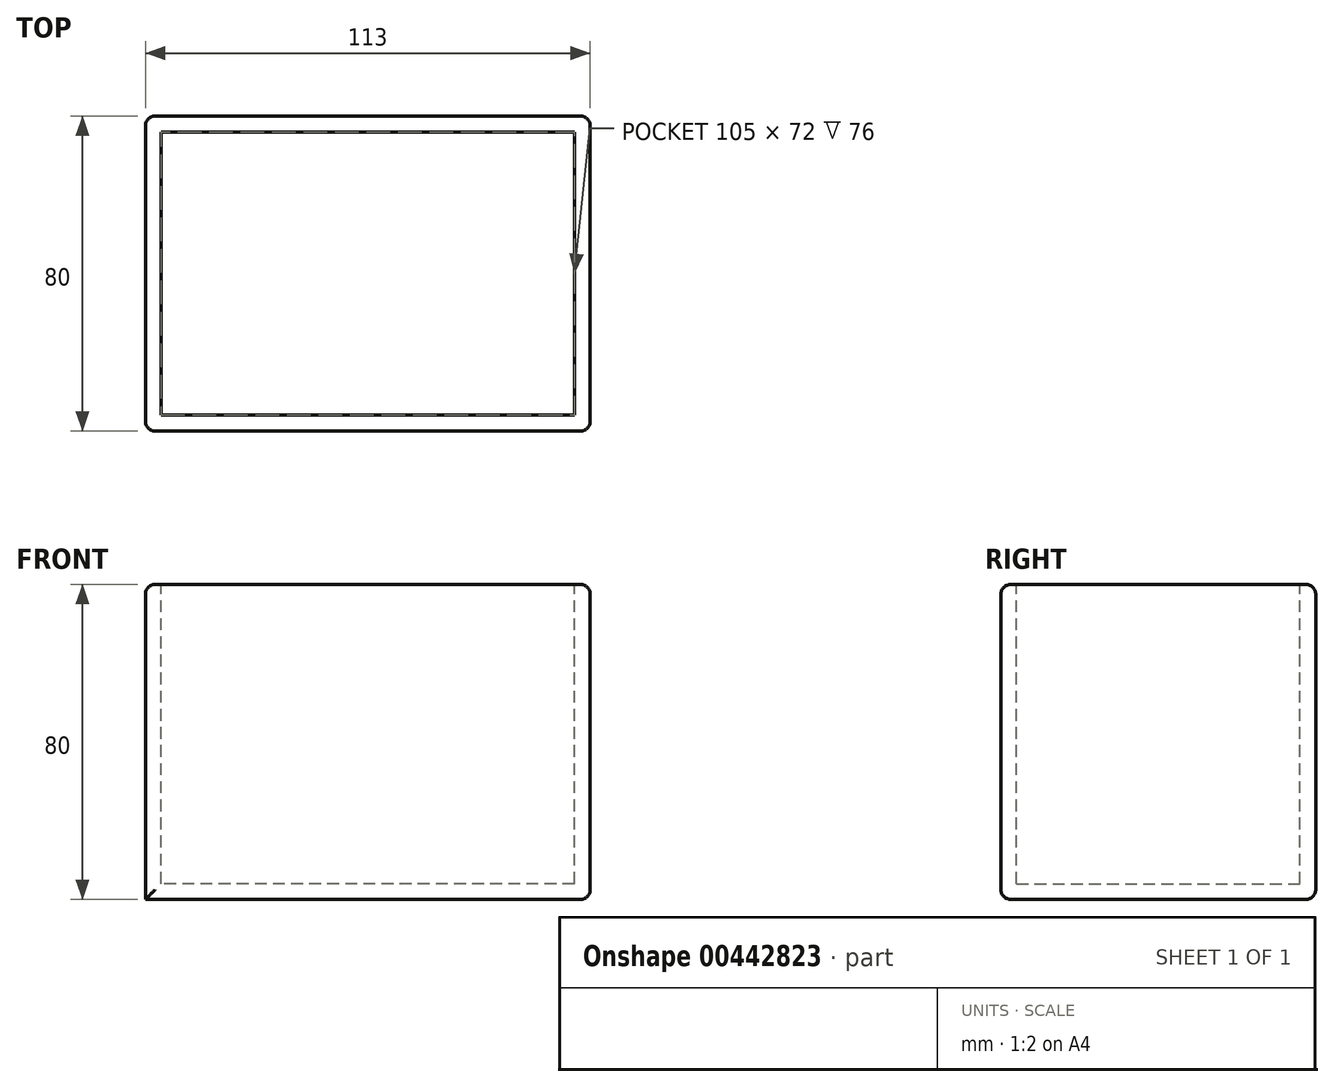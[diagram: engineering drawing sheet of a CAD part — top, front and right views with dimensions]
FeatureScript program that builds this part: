
annotation { "Feature Type Name" : "Feature", "Feature Type Description" : "" }
export const myFeature = defineFeature(function(context is Context, id is Id, definition is map)
    precondition{}
    {
        {
            var Q0;
            Q0=qCreatedBy(makeId("Front.planeOp"),FACE);
            var sketch = newSketch(context, id + "F0", { "sketchPlane" : qUnion([Q0])});
            skLineSegment(sketch, "E0.bottom", {"start": v(0, 0) * mm, "end": v(-113, 0) * mm});
            skLineSegment(sketch, "E0.top", {"start": v(0, 80) * mm, "end": v(-113, 80) * mm});
            skLineSegment(sketch, "E0.left", {"start": v(0, 0) * mm, "end": v(0, 80) * mm});
            skLineSegment(sketch, "E0.right", {"start": v(-113, 0) * mm, "end": v(-113, 80) * mm});
            skSolve(sketch);
        }
        {
            var Q0;
            Q0 = qSketchRegion(id + "F0", true);
            extrude(context, id + "F1", {"entities" : qUnion([Q0]), "depth" : 80 * mm, "offsetDistance" : 25 * mm});
        }
        {
            var Q0;
            Q0=makeQuery(id+"F1.opExtrude","SWEPT_FACE",FACE,{"disambiguationData":[OSD([sQuery(id+"F0.wireOp",EDGE,"E0.top")])]});
            shell(context, id + "F2", {"entities" : qUnion([Q0]), "thickness" : 4 * mm});
        }
        {
            var Q0;
            Q0=makeQuery(id+"F1.opExtrude","CAP_EDGE",EDGE,{"disambiguationData":[OSD([sQuery(id+"F0.wireOp",EDGE,"E0.left")])],"isStart":false});
            var Q1;
            Q1=makeQuery(id+"F1.opExtrude","CAP_EDGE",EDGE,{"disambiguationData":[OSD([sQuery(id+"F0.wireOp",EDGE,"E0.left")])],"isStart":true});
            var Q2;
            Q2=makeQuery(id+"F1.opExtrude","SWEPT_EDGE",EDGE,{"disambiguationData":[OSD([sQuery(id+"F0.wireOp",EDGE,"E0.top"),sQuery(id+"F0.wireOp",EDGE,"E0.left")])]});
            var Q3;
            Q3=makeQuery(id+"F1.opExtrude","CAP_EDGE",EDGE,{"disambiguationData":[OSD([sQuery(id+"F0.wireOp",EDGE,"E0.top")])],"isStart":false});
            var Q4;
            Q4=makeQuery(id+"F1.opExtrude","CAP_EDGE",EDGE,{"disambiguationData":[OSD([sQuery(id+"F0.wireOp",EDGE,"E0.top")])],"isStart":true});
            var Q5;
            Q5=makeQuery(id+"F1.opExtrude","CAP_EDGE",EDGE,{"disambiguationData":[OSD([sQuery(id+"F0.wireOp",EDGE,"E0.bottom")])],"isStart":false});
            var Q6;
            Q6=makeQuery(id+"F1.opExtrude","SWEPT_EDGE",EDGE,{"disambiguationData":[OSD([sQuery(id+"F0.wireOp",EDGE,"E0.bottom"),sQuery(id+"F0.wireOp",EDGE,"E0.left")])]});
            var Q7;
            Q7=makeQuery(id+"F1.opExtrude","CAP_EDGE",EDGE,{"disambiguationData":[OSD([sQuery(id+"F0.wireOp",EDGE,"E0.bottom")])],"isStart":true});
            var Q8;
            Q8=makeQuery(id+"F1.opExtrude","CAP_EDGE",EDGE,{"disambiguationData":[OSD([sQuery(id+"F0.wireOp",EDGE,"E0.right")])],"isStart":false});
            var Q9;
            Q9=makeQuery(id+"F1.opExtrude","CAP_EDGE",EDGE,{"disambiguationData":[OSD([sQuery(id+"F0.wireOp",EDGE,"E0.right")])],"isStart":true});
            var Q10;
            Q10=makeQuery(id+"F1.opExtrude","SWEPT_EDGE",EDGE,{"disambiguationData":[OSD([sQuery(id+"F0.wireOp",EDGE,"E0.top"),sQuery(id+"F0.wireOp",EDGE,"E0.right")])]});
            fillet(context, id + "F3", {"entities" : qUnion([Q0, Q1, Q2, Q3, Q4, Q5, Q6, Q7, Q8, Q9, Q10]), "radius" : 2.5 * mm, "tangentPropagation" : true, "allowEdgeOverflow" : false});
        }
    });
